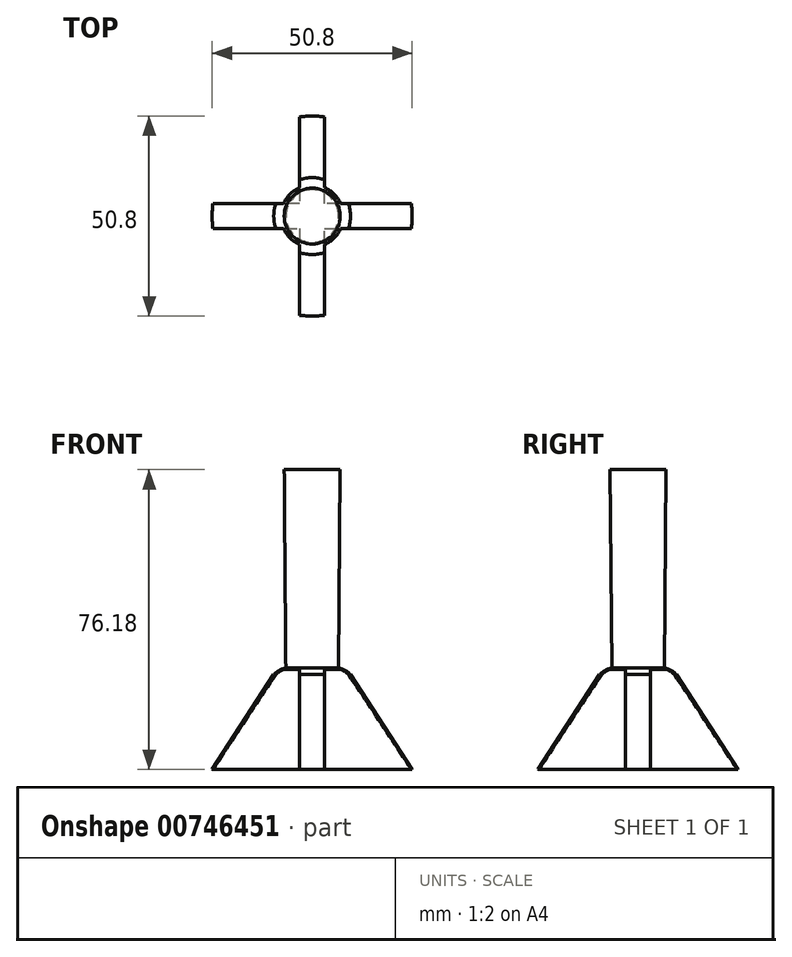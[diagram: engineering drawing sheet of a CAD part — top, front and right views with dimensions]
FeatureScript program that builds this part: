
annotation { "Feature Type Name" : "Feature", "Feature Type Description" : "" }
export const myFeature = defineFeature(function(context is Context, id is Id, definition is map)
    precondition{}
    {
        {
            var Q0;
            Q0=qCreatedBy(makeId("Front.planeOp"),FACE);
            var sketch = newSketch(context, id + "F0", { "sketchPlane" : qUnion([Q0])});
            skLineSegment(sketch, "E0", {"start": v(0, 0) * mm, "end": v(25.4, 0) * mm});
            skLineSegment(sketch, "E1", {"start": v(0, 0) * mm, "end": v(0, 25.4) * mm});
            skLineSegment(sketch, "E2", {"start": v(7.1, 76.18) * mm, "end": v(0, 76.18) * mm});
            skLineSegment(sketch, "E3", {"start": v(0, 76.18) * mm, "end": v(0, 25.4) * mm});
            skLineSegment(sketch, "E4", {"start": v(7.1, 76.18) * mm, "end": v(6.7, 25.8) * mm});
            skLineSegment(sketch, "E5", {"start": v(9.76, 24.07) * mm, "end": v(25.4, 0) * mm});
            skArc(sketch, "E6", {"start": v(6.7, 25.8) * mm, "mid": v(8.36, 25.17) * mm, "end": v(9.76, 24.07) * mm});
            skSolve(sketch);
        }
        {
            var Q0;
            Q0=makeQuery(id+"F0.imprint","IMPRINT",FACE,{"disambiguationData":[TD([[makeQuery(id+"F0.imprint","IMPRINT",EDGE,{"derivedFrom":sQuery(id+"F0.wireOp",EDGE,"E0")}),1.0]])]});
            var Q1;
            Q1=sQuery(id+"F0.wireOp",EDGE,"E1");
            revolve(context, id + "F1", {"surfaceOperationType" : NewSurfaceOperationType.NEW, "entities" : qUnion([Q0]), "axis" : qUnion([Q1]), "revolveType" : RevolveType.FULL});
        }
        {
            var Q0;
            Q0=qCreatedBy(makeId("Top.planeOp"),FACE);
            var sketch = newSketch(context, id + "F2", { "sketchPlane" : qUnion([Q0])});
            skLineSegment(sketch, "E7", {"start": v(3.18, -37.03) * mm, "end": v(3.17, -3.18) * mm});
            skLineSegment(sketch, "E8", {"start": v(3.17, -3.18) * mm, "end": v(37.03, -3.17) * mm});
            skLineSegment(sketch, "E9", {"start": v(37.17, 3.18) * mm, "end": v(3.18, 3.17) * mm});
            skLineSegment(sketch, "E10", {"start": v(3.18, 3.17) * mm, "end": v(3.18, 37.17) * mm});
            skLineSegment(sketch, "E11", {"start": v(-3.18, 36.79) * mm, "end": v(-3.17, 3.18) * mm});
            skLineSegment(sketch, "E12", {"start": v(-3.17, 3.18) * mm, "end": v(-36.79, 3.18) * mm});
            skLineSegment(sketch, "E13", {"start": v(-37.17, -3.18) * mm, "end": v(-3.18, -3.17) * mm});
            skLineSegment(sketch, "E14", {"start": v(-3.18, -3.17) * mm, "end": v(-3.17, -37.17) * mm});
            skArc(sketch, "E15", {"start": v(-36.79, 3.18) * mm, "mid": v(-26.1, 26.1) * mm, "end": v(-3.18, 36.79) * mm});
            skArc(sketch, "E16", {"start": v(37.17, 3.18) * mm, "mid": v(26.38, 26.38) * mm, "end": v(3.18, 37.17) * mm});
            skArc(sketch, "E17", {"start": v(3.18, -37.03) * mm, "mid": v(26.28, -26.28) * mm, "end": v(37.03, -3.17) * mm});
            skArc(sketch, "E18", {"start": v(-37.17, -3.18) * mm, "mid": v(-26.38, -26.38) * mm, "end": v(-3.17, -37.17) * mm});
            skSolve(sketch);
        }
        {
            var Q0;
            Q0 = qSketchRegion(id + "F2", true);
            extrude(context, id + "F3", {"entities" : qUnion([Q0]), "operationType" : NewBodyOperationType.REMOVE, "depth" : 25.4 * mm, "offsetDistance" : 25.4 * mm});
        }
    });
